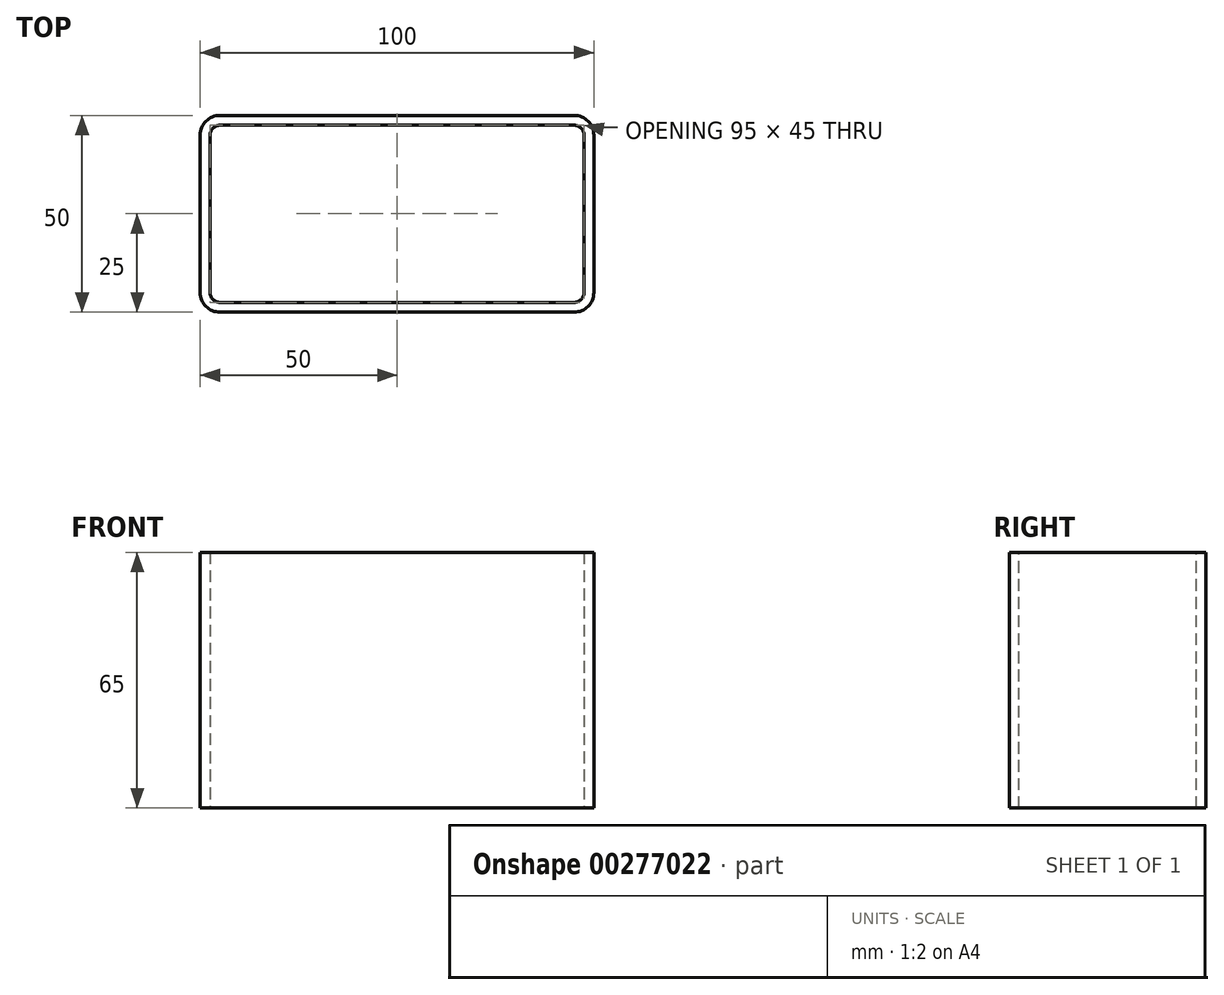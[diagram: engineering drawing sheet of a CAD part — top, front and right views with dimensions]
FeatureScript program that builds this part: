
annotation { "Feature Type Name" : "Feature", "Feature Type Description" : "" }
export const myFeature = defineFeature(function(context is Context, id is Id, definition is map)
    precondition{}
    {
        {
            var Q0;
            Q0=qCreatedBy(makeId("Front.planeOp"),FACE);
            var sketch = newSketch(context, id + "F0", { "sketchPlane" : qUnion([Q0])});
            skLineSegment(sketch, "E0.bottom", {"start": v(-50, 32.5) * mm, "end": v(50, 32.5) * mm});
            skLineSegment(sketch, "E0.top", {"start": v(-50, -32.5) * mm, "end": v(50, -32.5) * mm});
            skLineSegment(sketch, "E0.left", {"start": v(-50, 32.5) * mm, "end": v(-50, -32.5) * mm});
            skLineSegment(sketch, "E0.right", {"start": v(50, 32.5) * mm, "end": v(50, -32.5) * mm});
            skPoint(sketch, "E0.middle", {"position": v(0, 0) * mm});
            skSolve(sketch);
        }
        {
            var Q0;
            Q0 = qSketchRegion(id + "F0", true);
            extrude(context, id + "F1", {"entities" : qUnion([Q0]), "depth" : 50 * mm});
        }
        {
            var Q0;
            Q0=makeQuery(id+"F1.opExtrude","CAP_EDGE",EDGE,{"disambiguationData":[OSD([sQuery(id+"F0.wireOp",EDGE,"E0.left")])],"isStart":false});
            var Q1;
            Q1=makeQuery(id+"F1.opExtrude","CAP_EDGE",EDGE,{"disambiguationData":[OSD([sQuery(id+"F0.wireOp",EDGE,"E0.left")])],"isStart":true});
            var Q2;
            Q2=makeQuery(id+"F1.opExtrude","CAP_EDGE",EDGE,{"disambiguationData":[OSD([sQuery(id+"F0.wireOp",EDGE,"E0.right")])],"isStart":false});
            var Q3;
            Q3=makeQuery(id+"F1.opExtrude","CAP_EDGE",EDGE,{"disambiguationData":[OSD([sQuery(id+"F0.wireOp",EDGE,"E0.right")])],"isStart":true});
            fillet(context, id + "F2", {"entities" : qUnion([Q0, Q1, Q2, Q3]), "radius" : 5 * mm, "tangentPropagation" : true, "allowEdgeOverflow" : false});
        }
        {
            var Q0;
            Q0=makeQuery(id+"F1.opExtrude","SWEPT_FACE",FACE,{"disambiguationData":[OSD([sQuery(id+"F0.wireOp",EDGE,"E0.bottom")])]});
            var Q1;
            Q1=makeQuery(id+"F1.opExtrude","SWEPT_FACE",FACE,{"disambiguationData":[OSD([sQuery(id+"F0.wireOp",EDGE,"E0.top")])]});
            shell(context, id + "F3", {"entities" : qUnion([Q0, Q1]), "thickness" : 2.5 * mm});
        }
    });
